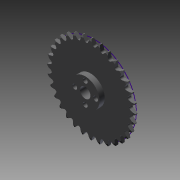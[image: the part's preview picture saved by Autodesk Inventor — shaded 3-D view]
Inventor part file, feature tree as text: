
AUTODESK INVENTOR PART (.ipt)
format: ipt  version: 2015 (Build 190159000, 159)  size: 753,152 bytes
history: native  units: in
note: dims shown in document units (in); Inventor stores cm internally (conversion verified against a paired STEP export)
features: other x14, sketch x1, imported_body x1
ambient origin geometry x8: Origin, YZ Plane, XZ Plane, XY Plane, X Axis, Y Axis, Z Axis, Center Point
bodies: Body1 (feature_tree)
feature tree (16):
  other  "tetrix_739171_2012"
  other  "tetrix_739171_20121"
  other  "A_1"
  other  "A_2"
  other  "A_4"
  other  "A_5"
  other  "A_3"
  other  "A_7"
  other  "A_8"
  other  "A_9"
  other  "A_6"
  other  "FRONT"
  other  "TOP"
  other  "RIGHT"
  sketch  "Sketch1"
  imported_body  "Base1"
